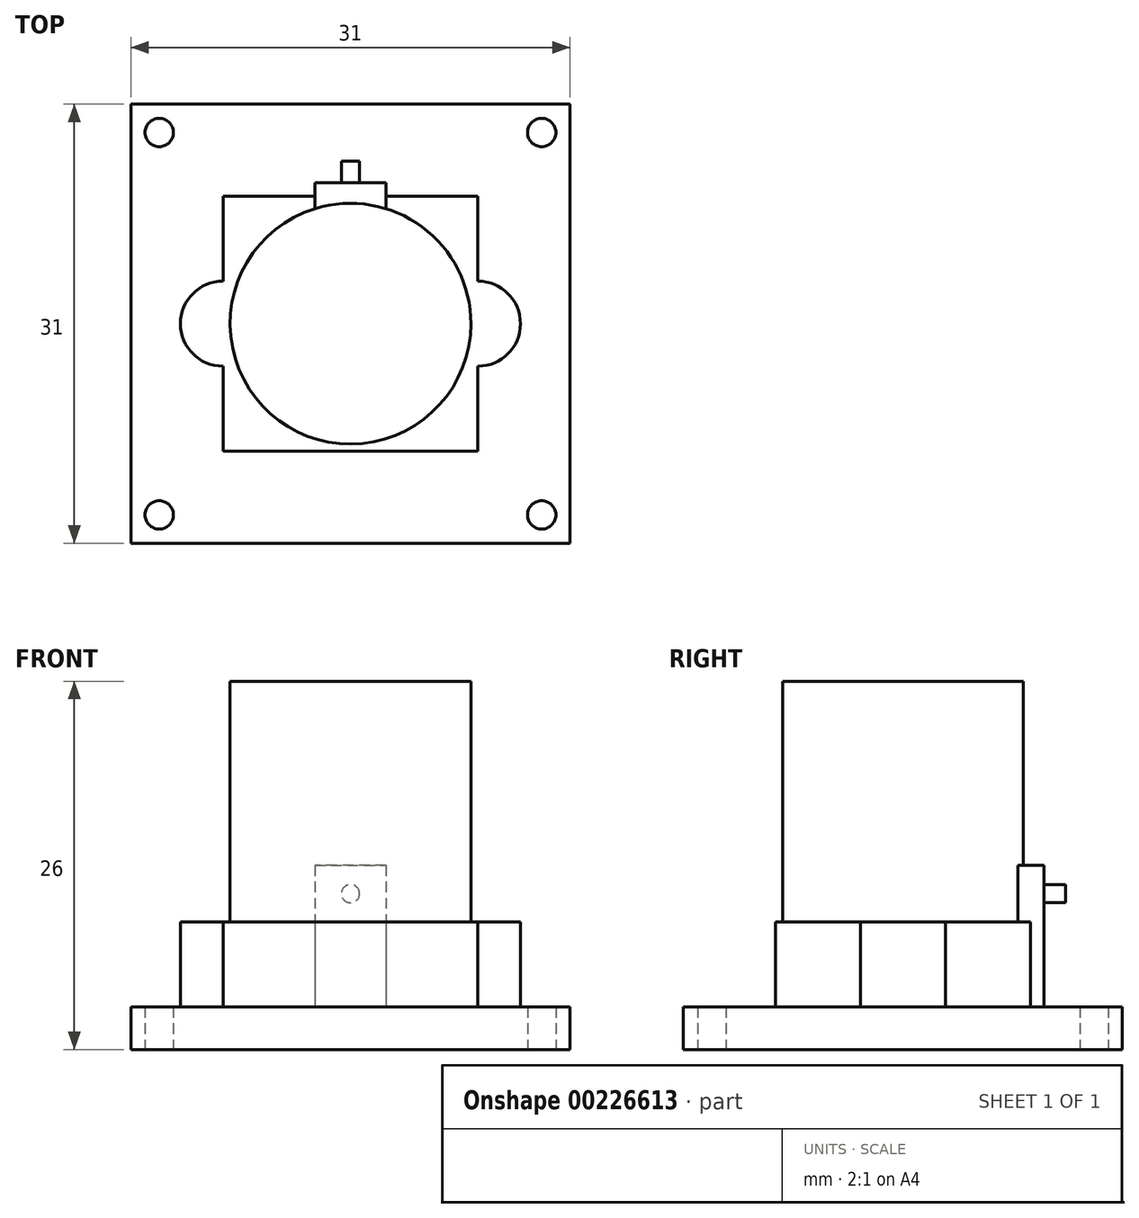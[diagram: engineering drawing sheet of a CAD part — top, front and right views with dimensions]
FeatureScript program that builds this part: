
annotation { "Feature Type Name" : "Feature", "Feature Type Description" : "" }
export const myFeature = defineFeature(function(context is Context, id is Id, definition is map)
    precondition{}
    {
        {
            var Q0;
            Q0=qCreatedBy(makeId("Top.planeOp"),FACE);
            var sketch = newSketch(context, id + "F0", { "sketchPlane" : qUnion([Q0])});
            skLineSegment(sketch, "E0.bottom", {"start": v(9, 11.36) * mm, "end": v(2.5, 11.36) * mm});
            skLineSegment(sketch, "E0.top", {"start": v(9, -6.64) * mm, "end": v(-9, -6.64) * mm});
            skLineSegment(sketch, "E0.left", {"start": v(9, 11.36) * mm, "end": v(9, 5.36) * mm});
            skLineSegment(sketch, "E0.right", {"start": v(-9, 11.36) * mm, "end": v(-9, 5.36) * mm});
            skArc(sketch, "E1", {"start": v(9, 5.36) * mm, "mid": v(12, 2.36) * mm, "end": v(9, -0.64) * mm});
            skArc(sketch, "E2.MirrorCS", {"start": v(-9, 5.36) * mm, "mid": v(-12, 2.36) * mm, "end": v(-9, -0.64) * mm});
            skCircle(sketch, "E3", {"center": v(0, 2.36) * mm, "radius": 8.5 * mm});
            skLineSegment(sketch, "E4", {"start": v(-2.5, 10.48) * mm, "end": v(-2.5, 12.33) * mm});
            skLineSegment(sketch, "E5", {"start": v(-2.5, 12.33) * mm, "end": v(2.5, 12.33) * mm});
            skLineSegment(sketch, "E6", {"start": v(-9, 2.36) * mm, "end": v(9, 2.36) * mm, "construction": true});
            skLineSegment(sketch, "E7", {"start": v(2.5, 12.33) * mm, "end": v(2.5, 10.48) * mm});
            skLineSegment(sketch, "E8.trimOffspring", {"start": v(-2.5, 11.36) * mm, "end": v(-9, 11.36) * mm});
            skLineSegment(sketch, "E9.trimOffspring", {"start": v(-9, -0.64) * mm, "end": v(-9, -6.64) * mm});
            skLineSegment(sketch, "E10.trimOffspring", {"start": v(9, -0.64) * mm, "end": v(9, -6.64) * mm});
            skLineSegment(sketch, "E11.bottom", {"start": v(15.5, -13.14) * mm, "end": v(-15.5, -13.14) * mm});
            skLineSegment(sketch, "E11.top", {"start": v(15.5, 17.86) * mm, "end": v(-15.5, 17.86) * mm});
            skLineSegment(sketch, "E11.left", {"start": v(15.5, -13.14) * mm, "end": v(15.5, 17.86) * mm});
            skLineSegment(sketch, "E11.right", {"start": v(-15.5, -13.14) * mm, "end": v(-15.5, 17.86) * mm});
            skCircle(sketch, "E12", {"center": v(13.5, 15.86) * mm, "radius": 1 * mm});
            skCircle(sketch, "E13", {"center": v(-13.5, 15.86) * mm, "radius": 1 * mm});
            skCircle(sketch, "E14", {"center": v(-13.5, -11.14) * mm, "radius": 1 * mm});
            skCircle(sketch, "E15", {"center": v(13.5, -11.14) * mm, "radius": 1 * mm});
            skSolve(sketch);
        }
        {
            var Q0;
            {var subQ2=sQuery(id+"F0.wireOp",EDGE,"E0.bottom");Q0=makeQuery(id+"F0.imprint","IMPRINT",FACE,{"disambiguationData":[TD([[makeQuery(id+"F0.imprint","IMPRINT",EDGE,{"derivedFrom":subQ2}),-1.0]])]});}
            extrude(context, id + "F1", {"entities" : qUnion([Q0]), "depth" : 3 * mm});
        }
        {
            var Q0;
            {var subQ0=sQuery(id+"F0.wireOp",EDGE,"E3");var subQ1=makeQuery(id+"F0.imprint","INTERSECT",VERTEX,{"derivedFrom":[subQ0,sQuery(id+"F0.wireOp",EDGE,"E4")]});Q0=makeQuery(id+"F0.imprint","IMPRINT",FACE,{"disambiguationData":[TD([[makeQuery(id+"F0.imprint","IMPRINT",EDGE,{"disambiguationData":[TD([[subQ1,1.0]])],"derivedFrom":subQ0}),1.0]])]});}
            extrude(context, id + "F2", {"entities" : qUnion([Q0]), "operationType" : NewBodyOperationType.ADD, "depth" : 26 * mm});
        }
        {
            var Q0;
            {var subQ6=sQuery(id+"F0.wireOp",EDGE,"E0.bottom");Q0=makeQuery(id+"F0.imprint","IMPRINT",FACE,{"disambiguationData":[TD([[makeQuery(id+"F0.imprint","IMPRINT",EDGE,{"derivedFrom":subQ6}),1.0]])]});}
            extrude(context, id + "F3", {"entities" : qUnion([Q0]), "operationType" : NewBodyOperationType.ADD, "depth" : 9 * mm});
        }
        {
            var Q0;
            {var subQ0=sQuery(id+"F0.wireOp",EDGE,"E5");Q0=makeQuery(id+"F0.imprint","IMPRINT",FACE,{"disambiguationData":[TD([[makeQuery(id+"F0.imprint","IMPRINT",EDGE,{"derivedFrom":subQ0}),-1.0]])]});}
            extrude(context, id + "F4", {"entities" : qUnion([Q0]), "operationType" : NewBodyOperationType.ADD, "depth" : 13 * mm});
        }
        {
            var Q0;
            Q0=makeQuery(id+"F4.opExtrude","SWEPT_FACE",FACE,{"disambiguationData":[OSD([sQuery(id+"F0.wireOp",EDGE,"E5")])]});
            var sketch = newSketch(context, id + "F5", { "sketchPlane" : qUnion([Q0])});
            skCircle(sketch, "E16", {"center": v(0, 11) * mm, "radius": 0.64 * mm});
            skSolve(sketch);
        }
        {
            var Q0;
            Q0=makeQuery(id+"F5.imprint","IMPRINT",FACE,{"disambiguationData":[TD([[makeQuery(id+"F5.imprint","IMPRINT",EDGE,{"derivedFrom":sQuery(id+"F5.wireOp",EDGE,"E16")}),1.0]])]});
            extrude(context, id + "F6", {"entities" : qUnion([Q0]), "operationType" : NewBodyOperationType.ADD, "depth" : 1.5 * mm});
        }
        {
            var Q0;
            Q0=makeQuery(id+"F1.opExtrude","SWEPT_BODY",BODY,{"disambiguationData":[OSD([sQuery(id+"F0.wireOp",EDGE,"E0.bottom"),sQuery(id+"F0.wireOp",EDGE,"E0.top"),sQuery(id+"F0.wireOp",EDGE,"E0.left"),sQuery(id+"F0.wireOp",EDGE,"E0.right"),sQuery(id+"F0.wireOp",EDGE,"E1"),sQuery(id+"F0.wireOp",EDGE,"E2.MirrorCS"),sQuery(id+"F0.wireOp",EDGE,"E4"),sQuery(id+"F0.wireOp",EDGE,"E5"),sQuery(id+"F0.wireOp",EDGE,"E7"),sQuery(id+"F0.wireOp",EDGE,"E8.trimOffspring"),sQuery(id+"F0.wireOp",EDGE,"E9.trimOffspring"),sQuery(id+"F0.wireOp",EDGE,"E10.trimOffspring"),sQuery(id+"F0.wireOp",EDGE,"E11.bottom"),sQuery(id+"F0.wireOp",EDGE,"E11.top"),sQuery(id+"F0.wireOp",EDGE,"E11.left"),sQuery(id+"F0.wireOp",EDGE,"E11.right"),sQuery(id+"F0.wireOp",EDGE,"E12"),sQuery(id+"F0.wireOp",EDGE,"E13"),sQuery(id+"F0.wireOp",EDGE,"E14"),sQuery(id+"F0.wireOp",EDGE,"E15")])]});
            transform(context, id + "F7", {"entities" : qUnion([Q0]), "transformType" : TransformType.TRANSLATION_3D, "dx" : 0 * mm, "dy" : 0 * mm, "dz" : 0 * mm, "makeCopy" : true});
        }
        {
            var Q0;
            Q0=makeQuery(id+"F7.opPattern","COPY",BODY,{"derivedFrom":makeQuery(id+"F1.opExtrude","SWEPT_BODY",BODY,{"disambiguationData":[OSD([sQuery(id+"F0.wireOp",EDGE,"E0.bottom"),sQuery(id+"F0.wireOp",EDGE,"E0.top"),sQuery(id+"F0.wireOp",EDGE,"E0.left"),sQuery(id+"F0.wireOp",EDGE,"E0.right"),sQuery(id+"F0.wireOp",EDGE,"E1"),sQuery(id+"F0.wireOp",EDGE,"E2.MirrorCS"),sQuery(id+"F0.wireOp",EDGE,"E4"),sQuery(id+"F0.wireOp",EDGE,"E5"),sQuery(id+"F0.wireOp",EDGE,"E7"),sQuery(id+"F0.wireOp",EDGE,"E8.trimOffspring"),sQuery(id+"F0.wireOp",EDGE,"E9.trimOffspring"),sQuery(id+"F0.wireOp",EDGE,"E10.trimOffspring"),sQuery(id+"F0.wireOp",EDGE,"E11.bottom"),sQuery(id+"F0.wireOp",EDGE,"E11.top"),sQuery(id+"F0.wireOp",EDGE,"E11.left"),sQuery(id+"F0.wireOp",EDGE,"E11.right"),sQuery(id+"F0.wireOp",EDGE,"E12"),sQuery(id+"F0.wireOp",EDGE,"E13"),sQuery(id+"F0.wireOp",EDGE,"E14"),sQuery(id+"F0.wireOp",EDGE,"E15")])]}),"instanceName":"1"});
            deleteBodies(context, id + "F8", {"entities" : qUnion([Q0])});
        }
    });
